# Revit family: Hager-GOLF-Flush_mounted-IP40-With_Cover-With_DIN-NoHosted-DE-de
name_source: partatom
category: Electrical Equipment
units: mm (PartAtom-declared; Revit-internal decimal feet)

## family parameters
Always vertical = Yes
Cut with Voids When Loaded = No
Maintain Annotation Orientation = No
Panel Configuration = Two Columns, Circuits Across
Part Type = Panelboard
Room Calculation Point = No
Round Connector Dimension = Use Diameter
Shared = No
Work Plane-Based = Yes

## types (69) — shared parameters
Code hager = ADD-EC000214_EU
Default Elevation = 1200 mm
EF000003 - Montageart = Unterputz
EF000007 - Farbe = weiß
EF000024 - UV-beständig = No
EF000049 - Tiefe = 97 mm  [stored 0.318241 ft]
EF000116 - RAL-Nummer = 9010
EF000118 - Mit Montageplatte = No
EF000218 - Einbautiefe = 72 mm  [stored 0.23622 ft]
EF001062 - EMV-Ausführung = No
EF001088 - Anbaumöglichkeit = Yes
EF001134 - DIN-Schiene = Yes
EF004462 - Art der Schließung = sonstige
EF005474 - Schutzart (IP) = IP40
EF006306 - Mit Schloss = No
EF009212 - Ausführung Deckel = geschlossen
EF015941 - Signaldurchlassende Tür = Yes
ETIM class code = EC000214
ETIM class name = Small distribution board
HG000001-Anzahl der Spalten = 1
HG000002-Mit tür = Yes
HG000003-Bereich = GOLF
HG000005-Dicke = 2 mm  [stored 0.00656168 ft]
HG000006-Flush mounted = Yes
HG000009-Doppelflügeligen Tür = No
HG000010-Asymmetrische Türen = No
HG000011-Leere Reihen von unten = No
HG000012-Türschwenkwinkel = 90.00°
HG000013-Tür links = No
HG000014-Tür rechts = Yes
HG000015-Sichtbarkeit der Türöffnung = Yes
HG000016-3D-Türsichtbarkeit = Yes
HG000017-Distanz zwischen den Polen = 18 mm  [stored 0.0590551 ft]
HG000060-RAL-number = 9010
HG000099-Onfly Template ID-de-DE = 507532
Manufacturer = Hager
Name BIM&CO = Electricity
Name hager = ADD_Enclosures_EC000214
Reference = Template-Enclosure_EU-EC000214
Uniformat = Low Tension Service & Dist.
Uniformat code = D501001
zero-valued in all types: EF001131 - Innentiefe, HG000007-Anzahl der leeren Spalten, HG000008-Anzahl der leeren Reihen

## per-type parameters (varying)
| type | BC_METADATA | EF000008 - Breite | EF000040 - Höhe | EF000266 - Anzahl der Reihen | EF000332 - Einbauhöhe | EF000846 - Einbaubreite | EF002950 - Breite in Teilungseinheiten | EF006244 - Transparenter Deckel/Tür | EF015776 - Erdungsklemmenblock | EF015777 - Neutralleiterklemmenblock | HG000004-Herstellerreferenz | HGEF000266-Anzahl der Reihen | HGEF0002950-Breite in Teilungseinheiten |
| GOLF-Flush_mounted_W204_H225_D97_4_Modular_Spacing-VF104PD | {"ObjectGuid":"2e7d348a-37d7-415c-a700-8c675d7a2511","ModelGuid":"d92884ee-31d5-45f1-a563-37bca790122f","VariantGuid":"b31a2e9c-c330-4702-bbce-c17fa995467c","Revision":"#5","VariantName":"GOLF-Flush_mounted_W204_H225_D97_4_Modular_Spacing-VF104PD"} | 204 mm | 225 mm  [stored 0.738189 ft] | 1 | 189 mm  [stored 0.620079 ft] | 170 mm  [stored 0.557743 ft] | 4 | No | Yes | Yes | VF104PD | 1 | 4 |
| GOLF-Flush_mounted_W204_H225_D97_4_Modular_Spacing-VF104PS | {"ObjectGuid":"2e7d348a-37d7-415c-a700-8c675d7a2511","ModelGuid":"d92884ee-31d5-45f1-a563-37bca790122f","VariantGuid":"cf317ba9-bf0b-43f1-8adb-6811de942370","Revision":"#5","VariantName":"GOLF-Flush_mounted_W204_H225_D97_4_Modular_Spacing-VF104PS"} | 204 mm | 225 mm  [stored 0.738189 ft] | 1 | 189 mm  [stored 0.620079 ft] | 170 mm  [stored 0.557743 ft] | 4 | No | No | No | VF104PS | 1 | 4 |
| GOLF-Flush_mounted_W204_H225_D97_4_Modular_Spacing-VF104TD | {"ObjectGuid":"2e7d348a-37d7-415c-a700-8c675d7a2511","ModelGuid":"d92884ee-31d5-45f1-a563-37bca790122f","VariantGuid":"4740b172-a5a6-4442-adbc-1241339a5770","Revision":"#5","VariantName":"GOLF-Flush_mounted_W204_H225_D97_4_Modular_Spacing-VF104TD"} | 204 mm | 225 mm  [stored 0.738189 ft] | 1 | 189 mm  [stored 0.620079 ft] | 170 mm  [stored 0.557743 ft] | 4 | Yes | Yes | Yes | VF104TD | 1 | 4 |
| GOLF-Flush_mounted_W204_H225_D97_4_Modular_Spacing-VF104TS | {"ObjectGuid":"2e7d348a-37d7-415c-a700-8c675d7a2511","ModelGuid":"d92884ee-31d5-45f1-a563-37bca790122f","VariantGuid":"b190a470-c8c2-49e1-a780-9f87e2cea34b","Revision":"#5","VariantName":"GOLF-Flush_mounted_W204_H225_D97_4_Modular_Spacing-VF104TS"} | 204 mm | 225 mm  [stored 0.738189 ft] | 1 | 189 mm  [stored 0.620079 ft] | 170 mm  [stored 0.557743 ft] | 4 | Yes | No | No | VF104TS | 1 | 4 |
| GOLF-Flush_mounted_W275_H225_D97_8_Modular_Spacing-VF108PA | {"ObjectGuid":"2e7d348a-37d7-415c-a700-8c675d7a2511","ModelGuid":"d92884ee-31d5-45f1-a563-37bca790122f","VariantGuid":"5aee5411-9867-4517-88c6-ba6237cbbf09","Revision":"#5","VariantName":"GOLF-Flush_mounted_W275_H225_D97_8_Modular_Spacing-VF108PA"} | 275 mm | 225 mm  [stored 0.738189 ft] | 1 | 189 mm  [stored 0.620079 ft] | 242 mm  [stored 0.793963 ft] | 8 | No | Yes | Yes | VF108PA | 1 | 8 |
| GOLF-Flush_mounted_W275_H225_D97_8_Modular_Spacing-VF108PD | {"ObjectGuid":"2e7d348a-37d7-415c-a700-8c675d7a2511","ModelGuid":"d92884ee-31d5-45f1-a563-37bca790122f","VariantGuid":"886cf811-8d76-449f-90a1-8f1109ad9289","Revision":"#5","VariantName":"GOLF-Flush_mounted_W275_H225_D97_8_Modular_Spacing-VF108PD"} | 275 mm | 225 mm  [stored 0.738189 ft] | 1 | 189 mm  [stored 0.620079 ft] | 242 mm  [stored 0.793963 ft] | 8 | No | Yes | Yes | VF108PD | 1 | 8 |
| GOLF-Flush_mounted_W275_H225_D97_8_Modular_Spacing-VF108PS | {"ObjectGuid":"2e7d348a-37d7-415c-a700-8c675d7a2511","ModelGuid":"d92884ee-31d5-45f1-a563-37bca790122f","VariantGuid":"b0350e41-627a-4a22-b8d4-8089ab5dced8","Revision":"#5","VariantName":"GOLF-Flush_mounted_W275_H225_D97_8_Modular_Spacing-VF108PS"} | 275 mm | 225 mm  [stored 0.738189 ft] | 1 | 189 mm  [stored 0.620079 ft] | 242 mm  [stored 0.793963 ft] | 8 | No | No | No | VF108PS | 1 | 8 |
| GOLF-Flush_mounted_W275_H225_D97_8_Modular_Spacing-VF108TA | {"ObjectGuid":"2e7d348a-37d7-415c-a700-8c675d7a2511","ModelGuid":"d92884ee-31d5-45f1-a563-37bca790122f","VariantGuid":"434fecd7-12d2-4bc4-95db-9da8fda5b05a","Revision":"#5","VariantName":"GOLF-Flush_mounted_W275_H225_D97_8_Modular_Spacing-VF108TA"} | 275 mm | 225 mm  [stored 0.738189 ft] | 1 | 189 mm  [stored 0.620079 ft] | 242 mm  [stored 0.793963 ft] | 8 | Yes | Yes | Yes | VF108TA | 1 | 8 |
| GOLF-Flush_mounted_W275_H225_D97_8_Modular_Spacing-VF108TD | {"ObjectGuid":"2e7d348a-37d7-415c-a700-8c675d7a2511","ModelGuid":"d92884ee-31d5-45f1-a563-37bca790122f","VariantGuid":"33042274-c18e-4c81-9396-54769ed373ac","Revision":"#5","VariantName":"GOLF-Flush_mounted_W275_H225_D97_8_Modular_Spacing-VF108TD"} | 275 mm | 225 mm  [stored 0.738189 ft] | 1 | 189 mm  [stored 0.620079 ft] | 242 mm  [stored 0.793963 ft] | 8 | Yes | Yes | Yes | VF108TD | 1 | 8 |
| GOLF-Flush_mounted_W275_H225_D97_8_Modular_Spacing-VF108TJ | {"ObjectGuid":"2e7d348a-37d7-415c-a700-8c675d7a2511","ModelGuid":"d92884ee-31d5-45f1-a563-37bca790122f","VariantGuid":"0d447c01-cd4f-45ee-b8f3-b86ee1e16cdc","Revision":"#5","VariantName":"GOLF-Flush_mounted_W275_H225_D97_8_Modular_Spacing-VF108TJ"} | 275 mm | 225 mm  [stored 0.738189 ft] | 1 | 189 mm  [stored 0.620079 ft] | 242 mm  [stored 0.793963 ft] | 8 | Yes | Yes | Yes | VF108TJ | 1 | 8 |
| GOLF-Flush_mounted_W275_H225_D97_8_Modular_Spacing-VF108TS | {"ObjectGuid":"2e7d348a-37d7-415c-a700-8c675d7a2511","ModelGuid":"d92884ee-31d5-45f1-a563-37bca790122f","VariantGuid":"a07ff41f-50ed-4bbd-adef-f6161eaefa04","Revision":"#5","VariantName":"GOLF-Flush_mounted_W275_H225_D97_8_Modular_Spacing-VF108TS"} | 275 mm | 225 mm  [stored 0.738189 ft] | 1 | 189 mm  [stored 0.620079 ft] | 242 mm  [stored 0.793963 ft] | 8 | Yes | No | No | VF108TS | 1 | 8 |
| GOLF-Flush_mounted_W352_H293_D97_12_Modular_Spacing-VF112PD | {"ObjectGuid":"2e7d348a-37d7-415c-a700-8c675d7a2511","ModelGuid":"d92884ee-31d5-45f1-a563-37bca790122f","VariantGuid":"0fa4f423-8072-41b0-9108-ada0960ab0c6","Revision":"#5","VariantName":"GOLF-Flush_mounted_W352_H293_D97_12_Modular_Spacing-VF112PD"} | 352 mm  [stored 1.15486 ft] | 293 mm | 1 | 257 mm  [stored 0.843176 ft] | 318 mm  [stored 1.04331 ft] | 12 | No | Yes | Yes | VF112PD | 1 | 12 |
| GOLF-Flush_mounted_W352_H293_D97_12_Modular_Spacing-VF112PF | {"ObjectGuid":"2e7d348a-37d7-415c-a700-8c675d7a2511","ModelGuid":"d92884ee-31d5-45f1-a563-37bca790122f","VariantGuid":"cda2493f-6014-4af5-b370-7196b7a504cb","Revision":"#5","VariantName":"GOLF-Flush_mounted_W352_H293_D97_12_Modular_Spacing-VF112PF"} | 352 mm  [stored 1.15486 ft] | 293 mm | 1 | 257 mm  [stored 0.843176 ft] | 318 mm  [stored 1.04331 ft] | 12 | No | Yes | No | VF112PF | 1 | 12 |
| GOLF-Flush_mounted_W352_H293_D97_12_Modular_Spacing-VF112PJ | {"ObjectGuid":"2e7d348a-37d7-415c-a700-8c675d7a2511","ModelGuid":"d92884ee-31d5-45f1-a563-37bca790122f","VariantGuid":"3e67deef-0626-41d4-b3ad-e567f991c98e","Revision":"#5","VariantName":"GOLF-Flush_mounted_W352_H293_D97_12_Modular_Spacing-VF112PJ"} | 352 mm  [stored 1.15486 ft] | 293 mm | 1 | 257 mm  [stored 0.843176 ft] | 318 mm  [stored 1.04331 ft] | 12 | No | Yes | Yes | VF112PJ | 1 | 12 |
| GOLF-Flush_mounted_W352_H293_D97_12_Modular_Spacing-VF112PS | {"ObjectGuid":"2e7d348a-37d7-415c-a700-8c675d7a2511","ModelGuid":"d92884ee-31d5-45f1-a563-37bca790122f","VariantGuid":"aa0eb0c4-cc24-4b40-a068-d6b0dbcf8f14","Revision":"#5","VariantName":"GOLF-Flush_mounted_W352_H293_D97_12_Modular_Spacing-VF112PS"} | 352 mm  [stored 1.15486 ft] | 293 mm | 1 | 257 mm  [stored 0.843176 ft] | 318 mm  [stored 1.04331 ft] | 12 | No | Yes | Yes | VF112PS | 1 | 12 |
| GOLF-Flush_mounted_W352_H293_D97_12_Modular_Spacing-VF112TD | {"ObjectGuid":"2e7d348a-37d7-415c-a700-8c675d7a2511","ModelGuid":"d92884ee-31d5-45f1-a563-37bca790122f","VariantGuid":"c066e9c2-883b-4a27-bd66-81f75bf34be1","Revision":"#5","VariantName":"GOLF-Flush_mounted_W352_H293_D97_12_Modular_Spacing-VF112TD"} | 352 mm  [stored 1.15486 ft] | 293 mm | 1 | 257 mm  [stored 0.843176 ft] | 318 mm  [stored 1.04331 ft] | 12 | Yes | Yes | Yes | VF112TD | 1 | 12 |
| GOLF-Flush_mounted_W352_H293_D97_12_Modular_Spacing-VF112TJ | {"ObjectGuid":"2e7d348a-37d7-415c-a700-8c675d7a2511","ModelGuid":"d92884ee-31d5-45f1-a563-37bca790122f","VariantGuid":"6bc9c1f8-911c-4ce2-a106-367671bf1206","Revision":"#5","VariantName":"GOLF-Flush_mounted_W352_H293_D97_12_Modular_Spacing-VF112TJ"} | 352 mm  [stored 1.15486 ft] | 293 mm | 1 | 257 mm  [stored 0.843176 ft] | 318 mm  [stored 1.04331 ft] | 12 | Yes | Yes | Yes | VF112TJ | 1 | 12 |
| GOLF-Flush_mounted_W352_H293_D97_12_Modular_Spacing-VF112TS | {"ObjectGuid":"2e7d348a-37d7-415c-a700-8c675d7a2511","ModelGuid":"d92884ee-31d5-45f1-a563-37bca790122f","VariantGuid":"ad58a622-cc60-446c-a541-a335049a2472","Revision":"#5","VariantName":"GOLF-Flush_mounted_W352_H293_D97_12_Modular_Spacing-VF112TS"} | 352 mm  [stored 1.15486 ft] | 293 mm | 1 | 257 mm  [stored 0.843176 ft] | 318 mm  [stored 1.04331 ft] | 12 | Yes | Yes | Yes | VF112TS | 1 | 12 |
| GOLF-Flush_mounted_W460_H293_D97_18_Modular_Spacing-VF118PD | {"ObjectGuid":"2e7d348a-37d7-415c-a700-8c675d7a2511","ModelGuid":"d92884ee-31d5-45f1-a563-37bca790122f","VariantGuid":"105932b2-cbf7-41df-8ac9-181a1f292d99","Revision":"#5","VariantName":"GOLF-Flush_mounted_W460_H293_D97_18_Modular_Spacing-VF118PD"} | 460 mm  [stored 1.50919 ft] | 293 mm | 1 | 257 mm  [stored 0.843176 ft] | 426 mm  [stored 1.39764 ft] | 18 | No | Yes | Yes | VF118PD | 1 | 18 |
| GOLF-Flush_mounted_W460_H293_D97_18_Modular_Spacing-VF118PJ | {"ObjectGuid":"2e7d348a-37d7-415c-a700-8c675d7a2511","ModelGuid":"d92884ee-31d5-45f1-a563-37bca790122f","VariantGuid":"70001ed9-ceb5-4983-a4dc-93935931aaab","Revision":"#5","VariantName":"GOLF-Flush_mounted_W460_H293_D97_18_Modular_Spacing-VF118PJ"} | 460 mm  [stored 1.50919 ft] | 293 mm | 1 | 257 mm  [stored 0.843176 ft] | 426 mm  [stored 1.39764 ft] | 18 | No | Yes | Yes | VF118PJ | 1 | 18 |
| GOLF-Flush_mounted_W460_H293_D97_18_Modular_Spacing-VF118PS | {"ObjectGuid":"2e7d348a-37d7-415c-a700-8c675d7a2511","ModelGuid":"d92884ee-31d5-45f1-a563-37bca790122f","VariantGuid":"d0a27ae8-1dc5-4747-8d64-8ad361803e2f","Revision":"#5","VariantName":"GOLF-Flush_mounted_W460_H293_D97_18_Modular_Spacing-VF118PS"} | 460 mm  [stored 1.50919 ft] | 293 mm | 1 | 257 mm  [stored 0.843176 ft] | 426 mm  [stored 1.39764 ft] | 18 | No | Yes | Yes | VF118PS | 1 | 18 |
| GOLF-Flush_mounted_W460_H293_D97_18_Modular_Spacing-VF118TD | {"ObjectGuid":"2e7d348a-37d7-415c-a700-8c675d7a2511","ModelGuid":"d92884ee-31d5-45f1-a563-37bca790122f","VariantGuid":"fbfa0a9f-1e1a-4261-a0f8-0ef638ea11ae","Revision":"#5","VariantName":"GOLF-Flush_mounted_W460_H293_D97_18_Modular_Spacing-VF118TD"} | 460 mm  [stored 1.50919 ft] | 293 mm | 1 | 257 mm  [stored 0.843176 ft] | 426 mm  [stored 1.39764 ft] | 18 | Yes | Yes | Yes | VF118TD | 1 | 18 |
| GOLF-Flush_mounted_W460_H293_D97_18_Modular_Spacing-VF118TJ | {"ObjectGuid":"2e7d348a-37d7-415c-a700-8c675d7a2511","ModelGuid":"d92884ee-31d5-45f1-a563-37bca790122f","VariantGuid":"94245f96-ff7b-4568-9343-245a51ee46bc","Revision":"#5","VariantName":"GOLF-Flush_mounted_W460_H293_D97_18_Modular_Spacing-VF118TJ"} | 460 mm  [stored 1.50919 ft] | 293 mm | 1 | 257 mm  [stored 0.843176 ft] | 426 mm  [stored 1.39764 ft] | 18 | Yes | Yes | Yes | VF118TJ | 1 | 18 |
| GOLF-Flush_mounted_W460_H293_D97_18_Modular_Spacing-VF118TS | {"ObjectGuid":"2e7d348a-37d7-415c-a700-8c675d7a2511","ModelGuid":"d92884ee-31d5-45f1-a563-37bca790122f","VariantGuid":"0d8941fe-6963-4aca-883e-c03dfea5f93c","Revision":"#5","VariantName":"GOLF-Flush_mounted_W460_H293_D97_18_Modular_Spacing-VF118TS"} | 460 mm  [stored 1.50919 ft] | 293 mm | 1 | 257 mm  [stored 0.843176 ft] | 426 mm  [stored 1.39764 ft] | 18 | Yes | Yes | Yes | VF118TS | 1 | 18 |
| GOLF-Flush_mounted_W532_H293_D97_22_Modular_Spacing-VF122PD | {"ObjectGuid":"2e7d348a-37d7-415c-a700-8c675d7a2511","ModelGuid":"d92884ee-31d5-45f1-a563-37bca790122f","VariantGuid":"ca360b59-2ed4-4731-9d1a-494a27b09c55","Revision":"#5","VariantName":"GOLF-Flush_mounted_W532_H293_D97_22_Modular_Spacing-VF122PD"} | 532 mm  [stored 1.74541 ft] | 293 mm | 1 | 257 mm  [stored 0.843176 ft] | 498 mm  [stored 1.63386 ft] | 22 | No | Yes | Yes | VF122PD | 1 | 22 |
| GOLF-Flush_mounted_W532_H293_D97_22_Modular_Spacing-VF122PJ | {"ObjectGuid":"2e7d348a-37d7-415c-a700-8c675d7a2511","ModelGuid":"d92884ee-31d5-45f1-a563-37bca790122f","VariantGuid":"9e92291c-d38c-4a34-8822-f9d752054a3e","Revision":"#5","VariantName":"GOLF-Flush_mounted_W532_H293_D97_22_Modular_Spacing-VF122PJ"} | 532 mm  [stored 1.74541 ft] | 293 mm | 1 | 257 mm  [stored 0.843176 ft] | 498 mm  [stored 1.63386 ft] | 22 | No | Yes | Yes | VF122PJ | 1 | 22 |
| GOLF-Flush_mounted_W532_H293_D97_22_Modular_Spacing-VF122PS | {"ObjectGuid":"2e7d348a-37d7-415c-a700-8c675d7a2511","ModelGuid":"d92884ee-31d5-45f1-a563-37bca790122f","VariantGuid":"727b1c2d-92bc-408c-a085-bd908a56903f","Revision":"#5","VariantName":"GOLF-Flush_mounted_W532_H293_D97_22_Modular_Spacing-VF122PS"} | 532 mm  [stored 1.74541 ft] | 293 mm | 1 | 257 mm  [stored 0.843176 ft] | 498 mm  [stored 1.63386 ft] | 22 | No | Yes | Yes | VF122PS | 1 | 22 |
| GOLF-Flush_mounted_W532_H293_D97_22_Modular_Spacing-VF122TD | {"ObjectGuid":"2e7d348a-37d7-415c-a700-8c675d7a2511","ModelGuid":"d92884ee-31d5-45f1-a563-37bca790122f","VariantGuid":"9d93141a-b6ba-4929-b79b-eee7cde6022e","Revision":"#5","VariantName":"GOLF-Flush_mounted_W532_H293_D97_22_Modular_Spacing-VF122TD"} | 532 mm  [stored 1.74541 ft] | 293 mm | 1 | 257 mm  [stored 0.843176 ft] | 498 mm  [stored 1.63386 ft] | 22 | Yes | Yes | Yes | VF122TD | 1 | 22 |
| GOLF-Flush_mounted_W532_H293_D97_22_Modular_Spacing-VF122TJ | {"ObjectGuid":"2e7d348a-37d7-415c-a700-8c675d7a2511","ModelGuid":"d92884ee-31d5-45f1-a563-37bca790122f","VariantGuid":"dadf0be1-38d8-4523-8671-6e9106750640","Revision":"#5","VariantName":"GOLF-Flush_mounted_W532_H293_D97_22_Modular_Spacing-VF122TJ"} | 532 mm  [stored 1.74541 ft] | 293 mm | 1 | 257 mm  [stored 0.843176 ft] | 498 mm  [stored 1.63386 ft] | 22 | Yes | Yes | Yes | VF122TJ | 1 | 22 |
| GOLF-Flush_mounted_W532_H293_D97_22_Modular_Spacing-VF122TS | {"ObjectGuid":"2e7d348a-37d7-415c-a700-8c675d7a2511","ModelGuid":"d92884ee-31d5-45f1-a563-37bca790122f","VariantGuid":"bc3eb722-4a62-46bc-8f7d-958ac2879342","Revision":"#5","VariantName":"GOLF-Flush_mounted_W532_H293_D97_22_Modular_Spacing-VF122TS"} | 532 mm  [stored 1.74541 ft] | 293 mm | 1 | 257 mm  [stored 0.843176 ft] | 498 mm  [stored 1.63386 ft] | 22 | Yes | Yes | Yes | VF122TS | 1 | 22 |
| GOLF-Flush_mounted_W382_H418_D97_12_Modular_Spacing-VF212PD | {"ObjectGuid":"2e7d348a-37d7-415c-a700-8c675d7a2511","ModelGuid":"d92884ee-31d5-45f1-a563-37bca790122f","VariantGuid":"98662327-9122-4b4b-b095-2d9bc4e226c7","Revision":"#5","VariantName":"GOLF-Flush_mounted_W382_H418_D97_12_Modular_Spacing-VF212PD"} | 382 mm  [stored 1.25328 ft] | 418 mm  [stored 1.37139 ft] | 2 | 382 mm  [stored 1.25328 ft] | 318 mm  [stored 1.04331 ft] | 12 | No | Yes | Yes | VF212PD | 2 | 12 |
| GOLF-Flush_mounted_W382_H418_D97_12_Modular_Spacing-VF212PF | {"ObjectGuid":"2e7d348a-37d7-415c-a700-8c675d7a2511","ModelGuid":"d92884ee-31d5-45f1-a563-37bca790122f","VariantGuid":"4c255126-cffe-43da-86a0-3f511cb3c73b","Revision":"#5","VariantName":"GOLF-Flush_mounted_W382_H418_D97_12_Modular_Spacing-VF212PF"} | 382 mm  [stored 1.25328 ft] | 418 mm  [stored 1.37139 ft] | 2 | 382 mm  [stored 1.25328 ft] | 318 mm  [stored 1.04331 ft] | 12 | No | Yes | No | VF212PF | 2 | 12 |
| GOLF-Flush_mounted_W382_H418_D97_12_Modular_Spacing-VF212PJ | {"ObjectGuid":"2e7d348a-37d7-415c-a700-8c675d7a2511","ModelGuid":"d92884ee-31d5-45f1-a563-37bca790122f","VariantGuid":"0282bb31-53a3-40e4-a5f7-7024e7f81640","Revision":"#5","VariantName":"GOLF-Flush_mounted_W382_H418_D97_12_Modular_Spacing-VF212PJ"} | 382 mm  [stored 1.25328 ft] | 418 mm  [stored 1.37139 ft] | 2 | 382 mm  [stored 1.25328 ft] | 318 mm  [stored 1.04331 ft] | 12 | No | Yes | Yes | VF212PJ | 2 | 12 |
| GOLF-Flush_mounted_W382_H418_D97_12_Modular_Spacing-VF212PS | {"ObjectGuid":"2e7d348a-37d7-415c-a700-8c675d7a2511","ModelGuid":"d92884ee-31d5-45f1-a563-37bca790122f","VariantGuid":"ee81c795-a8c6-4e0b-ac30-7d2952e06c4c","Revision":"#5","VariantName":"GOLF-Flush_mounted_W382_H418_D97_12_Modular_Spacing-VF212PS"} | 382 mm  [stored 1.25328 ft] | 418 mm  [stored 1.37139 ft] | 2 | 382 mm  [stored 1.25328 ft] | 318 mm  [stored 1.04331 ft] | 12 | No | Yes | Yes | VF212PS | 2 | 12 |
| GOLF-Flush_mounted_W382_H418_D97_12_Modular_Spacing-VF212TA | {"ObjectGuid":"2e7d348a-37d7-415c-a700-8c675d7a2511","ModelGuid":"d92884ee-31d5-45f1-a563-37bca790122f","VariantGuid":"6bae1c2d-9032-4d60-8b30-56f41d07c7fb","Revision":"#5","VariantName":"GOLF-Flush_mounted_W382_H418_D97_12_Modular_Spacing-VF212TA"} | 382 mm  [stored 1.25328 ft] | 418 mm  [stored 1.37139 ft] | 2 | 382 mm  [stored 1.25328 ft] | 318 mm  [stored 1.04331 ft] | 12 | Yes | Yes | Yes | VF212TA | 2 | 12 |
| GOLF-Flush_mounted_W382_H418_D97_12_Modular_Spacing-VF212TD | {"ObjectGuid":"2e7d348a-37d7-415c-a700-8c675d7a2511","ModelGuid":"d92884ee-31d5-45f1-a563-37bca790122f","VariantGuid":"fe428a60-72be-47c5-b277-cfdae7ead9f2","Revision":"#5","VariantName":"GOLF-Flush_mounted_W382_H418_D97_12_Modular_Spacing-VF212TD"} | 382 mm  [stored 1.25328 ft] | 418 mm  [stored 1.37139 ft] | 2 | 382 mm  [stored 1.25328 ft] | 318 mm  [stored 1.04331 ft] | 12 | Yes | Yes | Yes | VF212TD | 2 | 12 |
| GOLF-Flush_mounted_W382_H418_D97_12_Modular_Spacing-VF212TJ | {"ObjectGuid":"2e7d348a-37d7-415c-a700-8c675d7a2511","ModelGuid":"d92884ee-31d5-45f1-a563-37bca790122f","VariantGuid":"4d1ea7fb-c5ff-44ed-a8ff-c7a03550a839","Revision":"#5","VariantName":"GOLF-Flush_mounted_W382_H418_D97_12_Modular_Spacing-VF212TJ"} | 382 mm  [stored 1.25328 ft] | 418 mm  [stored 1.37139 ft] | 2 | 382 mm  [stored 1.25328 ft] | 318 mm  [stored 1.04331 ft] | 12 | Yes | Yes | Yes | VF212TJ | 2 | 12 |
| GOLF-Flush_mounted_W382_H418_D97_12_Modular_Spacing-VF212TS | {"ObjectGuid":"2e7d348a-37d7-415c-a700-8c675d7a2511","ModelGuid":"d92884ee-31d5-45f1-a563-37bca790122f","VariantGuid":"0f97c2f5-fb0b-4114-b1b1-1e9c94daf7b6","Revision":"#5","VariantName":"GOLF-Flush_mounted_W382_H418_D97_12_Modular_Spacing-VF212TS"} | 382 mm  [stored 1.25328 ft] | 418 mm  [stored 1.37139 ft] | 2 | 382 mm  [stored 1.25328 ft] | 318 mm  [stored 1.04331 ft] | 12 | Yes | Yes | Yes | VF212TS | 2 | 12 |
| GOLF-Flush_mounted_W460_H418_D97_18_Modular_Spacing-VF218PD | {"ObjectGuid":"2e7d348a-37d7-415c-a700-8c675d7a2511","ModelGuid":"d92884ee-31d5-45f1-a563-37bca790122f","VariantGuid":"99250fe5-2cb4-4589-b5fd-ac7613f56618","Revision":"#5","VariantName":"GOLF-Flush_mounted_W460_H418_D97_18_Modular_Spacing-VF218PD"} | 460 mm  [stored 1.50919 ft] | 418 mm  [stored 1.37139 ft] | 2 | 382 mm  [stored 1.25328 ft] | 426 mm  [stored 1.39764 ft] | 18 | No | Yes | Yes | VF218PD | 2 | 18 |
| GOLF-Flush_mounted_W460_H418_D97_18_Modular_Spacing-VF218PJ | {"ObjectGuid":"2e7d348a-37d7-415c-a700-8c675d7a2511","ModelGuid":"d92884ee-31d5-45f1-a563-37bca790122f","VariantGuid":"c85930e7-9cfc-47db-97e7-0fb22923e959","Revision":"#5","VariantName":"GOLF-Flush_mounted_W460_H418_D97_18_Modular_Spacing-VF218PJ"} | 460 mm  [stored 1.50919 ft] | 418 mm  [stored 1.37139 ft] | 2 | 382 mm  [stored 1.25328 ft] | 426 mm  [stored 1.39764 ft] | 18 | No | Yes | Yes | VF218PJ | 2 | 18 |
| GOLF-Flush_mounted_W460_H418_D97_18_Modular_Spacing-VF218PS | {"ObjectGuid":"2e7d348a-37d7-415c-a700-8c675d7a2511","ModelGuid":"d92884ee-31d5-45f1-a563-37bca790122f","VariantGuid":"cbc02418-1134-4bb1-abc3-8cda3f068379","Revision":"#5","VariantName":"GOLF-Flush_mounted_W460_H418_D97_18_Modular_Spacing-VF218PS"} | 460 mm  [stored 1.50919 ft] | 418 mm  [stored 1.37139 ft] | 2 | 382 mm  [stored 1.25328 ft] | 426 mm  [stored 1.39764 ft] | 18 | No | Yes | Yes | VF218PS | 2 | 18 |
| GOLF-Flush_mounted_W460_H418_D97_18_Modular_Spacing-VF218TD | {"ObjectGuid":"2e7d348a-37d7-415c-a700-8c675d7a2511","ModelGuid":"d92884ee-31d5-45f1-a563-37bca790122f","VariantGuid":"913d6e5d-7559-403e-89d5-0aa80b5e0efb","Revision":"#5","VariantName":"GOLF-Flush_mounted_W460_H418_D97_18_Modular_Spacing-VF218TD"} | 460 mm  [stored 1.50919 ft] | 418 mm  [stored 1.37139 ft] | 2 | 382 mm  [stored 1.25328 ft] | 426 mm  [stored 1.39764 ft] | 18 | Yes | Yes | Yes | VF218TD | 2 | 18 |
| GOLF-Flush_mounted_W460_H418_D97_18_Modular_Spacing-VF218TJ | {"ObjectGuid":"2e7d348a-37d7-415c-a700-8c675d7a2511","ModelGuid":"d92884ee-31d5-45f1-a563-37bca790122f","VariantGuid":"6aa5c099-a717-4ea1-8fc0-bc053faefae9","Revision":"#5","VariantName":"GOLF-Flush_mounted_W460_H418_D97_18_Modular_Spacing-VF218TJ"} | 460 mm  [stored 1.50919 ft] | 418 mm  [stored 1.37139 ft] | 2 | 382 mm  [stored 1.25328 ft] | 426 mm  [stored 1.39764 ft] | 18 | Yes | Yes | Yes | VF218TJ | 2 | 18 |
| GOLF-Flush_mounted_W460_H418_D97_18_Modular_Spacing-VF218TS | {"ObjectGuid":"2e7d348a-37d7-415c-a700-8c675d7a2511","ModelGuid":"d92884ee-31d5-45f1-a563-37bca790122f","VariantGuid":"8aefd23b-b0b6-4d46-847b-f36bf3c04371","Revision":"#5","VariantName":"GOLF-Flush_mounted_W460_H418_D97_18_Modular_Spacing-VF218TS"} | 460 mm  [stored 1.50919 ft] | 418 mm  [stored 1.37139 ft] | 2 | 382 mm  [stored 1.25328 ft] | 426 mm  [stored 1.39764 ft] | 18 | Yes | Yes | Yes | VF218TS | 2 | 18 |
| GOLF-Flush_mounted_W352_H543_D97_12_Modular_Spacing-VF312PD | {"ObjectGuid":"2e7d348a-37d7-415c-a700-8c675d7a2511","ModelGuid":"d92884ee-31d5-45f1-a563-37bca790122f","VariantGuid":"928b9372-45b5-4d68-aaf5-065da6247f86","Revision":"#5","VariantName":"GOLF-Flush_mounted_W352_H543_D97_12_Modular_Spacing-VF312PD"} | 352 mm  [stored 1.15486 ft] | 543 mm  [stored 1.7815 ft] | 3 | 507 mm  [stored 1.66339 ft] | 318 mm  [stored 1.04331 ft] | 12 | No | Yes | Yes | VF312PD | 3 | 12 |
| GOLF-Flush_mounted_W352_H543_D97_12_Modular_Spacing-VF312PF | {"ObjectGuid":"2e7d348a-37d7-415c-a700-8c675d7a2511","ModelGuid":"d92884ee-31d5-45f1-a563-37bca790122f","VariantGuid":"b4990f75-6e65-45c0-bd5a-b16e10202182","Revision":"#5","VariantName":"GOLF-Flush_mounted_W352_H543_D97_12_Modular_Spacing-VF312PF"} | 352 mm  [stored 1.15486 ft] | 543 mm  [stored 1.7815 ft] | 3 | 507 mm  [stored 1.66339 ft] | 318 mm  [stored 1.04331 ft] | 12 | No | Yes | No | VF312PF | 3 | 12 |
| GOLF-Flush_mounted_W352_H543_D97_12_Modular_Spacing-VF312PJ | {"ObjectGuid":"2e7d348a-37d7-415c-a700-8c675d7a2511","ModelGuid":"d92884ee-31d5-45f1-a563-37bca790122f","VariantGuid":"a1a3ce38-9ed2-44bf-af35-44c8f29b8579","Revision":"#5","VariantName":"GOLF-Flush_mounted_W352_H543_D97_12_Modular_Spacing-VF312PJ"} | 352 mm  [stored 1.15486 ft] | 543 mm  [stored 1.7815 ft] | 3 | 507 mm  [stored 1.66339 ft] | 318 mm  [stored 1.04331 ft] | 12 | No | Yes | Yes | VF312PJ | 3 | 12 |
| GOLF-Flush_mounted_W352_H543_D97_12_Modular_Spacing-VF312PS | {"ObjectGuid":"2e7d348a-37d7-415c-a700-8c675d7a2511","ModelGuid":"d92884ee-31d5-45f1-a563-37bca790122f","VariantGuid":"8e26eca7-dae5-4654-a159-605baed50f82","Revision":"#5","VariantName":"GOLF-Flush_mounted_W352_H543_D97_12_Modular_Spacing-VF312PS"} | 352 mm  [stored 1.15486 ft] | 543 mm  [stored 1.7815 ft] | 3 | 507 mm  [stored 1.66339 ft] | 318 mm  [stored 1.04331 ft] | 12 | No | Yes | Yes | VF312PS | 3 | 12 |
| GOLF-Flush_mounted_W352_H543_D97_12_Modular_Spacing-VF312TD | {"ObjectGuid":"2e7d348a-37d7-415c-a700-8c675d7a2511","ModelGuid":"d92884ee-31d5-45f1-a563-37bca790122f","VariantGuid":"48a651ff-040d-4527-aaab-b8df4a12e4b1","Revision":"#5","VariantName":"GOLF-Flush_mounted_W352_H543_D97_12_Modular_Spacing-VF312TD"} | 352 mm  [stored 1.15486 ft] | 543 mm  [stored 1.7815 ft] | 3 | 507 mm  [stored 1.66339 ft] | 318 mm  [stored 1.04331 ft] | 12 | Yes | Yes | Yes | VF312TD | 3 | 12 |
| GOLF-Flush_mounted_W352_H543_D97_12_Modular_Spacing-VF312TJ | {"ObjectGuid":"2e7d348a-37d7-415c-a700-8c675d7a2511","ModelGuid":"d92884ee-31d5-45f1-a563-37bca790122f","VariantGuid":"5769b36b-8467-4e38-b90c-6bff2941fc0c","Revision":"#5","VariantName":"GOLF-Flush_mounted_W352_H543_D97_12_Modular_Spacing-VF312TJ"} | 352 mm  [stored 1.15486 ft] | 543 mm  [stored 1.7815 ft] | 3 | 507 mm  [stored 1.66339 ft] | 318 mm  [stored 1.04331 ft] | 12 | Yes | Yes | Yes | VF312TJ | 3 | 12 |
| GOLF-Flush_mounted_W352_H543_D97_12_Modular_Spacing-VF312TS | {"ObjectGuid":"2e7d348a-37d7-415c-a700-8c675d7a2511","ModelGuid":"d92884ee-31d5-45f1-a563-37bca790122f","VariantGuid":"65151222-fdd9-4b8f-85c7-0e54bdfdcd5f","Revision":"#5","VariantName":"GOLF-Flush_mounted_W352_H543_D97_12_Modular_Spacing-VF312TS"} | 352 mm  [stored 1.15486 ft] | 543 mm  [stored 1.7815 ft] | 3 | 507 mm  [stored 1.66339 ft] | 318 mm  [stored 1.04331 ft] | 12 | Yes | Yes | Yes | VF312TS | 3 | 12 |
| GOLF-Flush_mounted_W460_H543_D97_18_Modular_Spacing-VF318PD | {"ObjectGuid":"2e7d348a-37d7-415c-a700-8c675d7a2511","ModelGuid":"d92884ee-31d5-45f1-a563-37bca790122f","VariantGuid":"9ea6dfa0-d29b-4304-aee7-7a29b1dce99d","Revision":"#5","VariantName":"GOLF-Flush_mounted_W460_H543_D97_18_Modular_Spacing-VF318PD"} | 460 mm  [stored 1.50919 ft] | 543 mm  [stored 1.7815 ft] | 3 | 507 mm  [stored 1.66339 ft] | 426 mm  [stored 1.39764 ft] | 18 | No | Yes | Yes | VF318PD | 3 | 18 |
| GOLF-Flush_mounted_W460_H543_D97_18_Modular_Spacing-VF318PJ | {"ObjectGuid":"2e7d348a-37d7-415c-a700-8c675d7a2511","ModelGuid":"d92884ee-31d5-45f1-a563-37bca790122f","VariantGuid":"5d8ebd72-7322-4c37-a4d5-e73088a7ca38","Revision":"#5","VariantName":"GOLF-Flush_mounted_W460_H543_D97_18_Modular_Spacing-VF318PJ"} | 460 mm  [stored 1.50919 ft] | 543 mm  [stored 1.7815 ft] | 3 | 507 mm  [stored 1.66339 ft] | 426 mm  [stored 1.39764 ft] | 18 | No | Yes | Yes | VF318PJ | 3 | 18 |
| GOLF-Flush_mounted_W460_H543_D97_18_Modular_Spacing-VF318PS | {"ObjectGuid":"2e7d348a-37d7-415c-a700-8c675d7a2511","ModelGuid":"d92884ee-31d5-45f1-a563-37bca790122f","VariantGuid":"5c6ad0df-804f-4d99-90e6-483a27ba6c35","Revision":"#5","VariantName":"GOLF-Flush_mounted_W460_H543_D97_18_Modular_Spacing-VF318PS"} | 460 mm  [stored 1.50919 ft] | 543 mm  [stored 1.7815 ft] | 3 | 507 mm  [stored 1.66339 ft] | 426 mm  [stored 1.39764 ft] | 18 | No | Yes | Yes | VF318PS | 3 | 18 |
| GOLF-Flush_mounted_W460_H543_D97_18_Modular_Spacing-VF318TD | {"ObjectGuid":"2e7d348a-37d7-415c-a700-8c675d7a2511","ModelGuid":"d92884ee-31d5-45f1-a563-37bca790122f","VariantGuid":"2c1dced4-bc37-4385-aeb4-8b4dd030778b","Revision":"#5","VariantName":"GOLF-Flush_mounted_W460_H543_D97_18_Modular_Spacing-VF318TD"} | 460 mm  [stored 1.50919 ft] | 543 mm  [stored 1.7815 ft] | 3 | 507 mm  [stored 1.66339 ft] | 426 mm  [stored 1.39764 ft] | 18 | Yes | Yes | Yes | VF318TD | 3 | 18 |
| GOLF-Flush_mounted_W460_H543_D97_18_Modular_Spacing-VF318TJ | {"ObjectGuid":"2e7d348a-37d7-415c-a700-8c675d7a2511","ModelGuid":"d92884ee-31d5-45f1-a563-37bca790122f","VariantGuid":"ca397d7b-ebee-4cf5-97ee-819891202b1a","Revision":"#5","VariantName":"GOLF-Flush_mounted_W460_H543_D97_18_Modular_Spacing-VF318TJ"} | 460 mm  [stored 1.50919 ft] | 543 mm  [stored 1.7815 ft] | 3 | 507 mm  [stored 1.66339 ft] | 426 mm  [stored 1.39764 ft] | 18 | Yes | Yes | Yes | VF318TJ | 3 | 18 |
| GOLF-Flush_mounted_W460_H543_D97_18_Modular_Spacing-VF318TS | {"ObjectGuid":"2e7d348a-37d7-415c-a700-8c675d7a2511","ModelGuid":"d92884ee-31d5-45f1-a563-37bca790122f","VariantGuid":"1c01b16a-0508-4a68-8f02-c14734786524","Revision":"#5","VariantName":"GOLF-Flush_mounted_W460_H543_D97_18_Modular_Spacing-VF318TS"} | 460 mm  [stored 1.50919 ft] | 543 mm  [stored 1.7815 ft] | 3 | 507 mm  [stored 1.66339 ft] | 426 mm  [stored 1.39764 ft] | 18 | Yes | Yes | Yes | VF318TS | 3 | 18 |
| GOLF-Flush_mounted_W352_H688_D97_12_Modular_Spacing-VF412PD | {"ObjectGuid":"2e7d348a-37d7-415c-a700-8c675d7a2511","ModelGuid":"d92884ee-31d5-45f1-a563-37bca790122f","VariantGuid":"49474903-83eb-41eb-8513-ab2748865e8c","Revision":"#5","VariantName":"GOLF-Flush_mounted_W352_H688_D97_12_Modular_Spacing-VF412PD"} | 352 mm  [stored 1.15486 ft] | 688 mm  [stored 2.25722 ft] | 4 | 652 mm  [stored 2.13911 ft] | 318 mm  [stored 1.04331 ft] | 12 | No | Yes | Yes | VF412PD | 4 | 12 |
| GOLF-Flush_mounted_W352_H688_D97_12_Modular_Spacing-VF412PJ | {"ObjectGuid":"2e7d348a-37d7-415c-a700-8c675d7a2511","ModelGuid":"d92884ee-31d5-45f1-a563-37bca790122f","VariantGuid":"23207760-10b2-4df7-90f7-609229f90366","Revision":"#5","VariantName":"GOLF-Flush_mounted_W352_H688_D97_12_Modular_Spacing-VF412PJ"} | 352 mm  [stored 1.15486 ft] | 688 mm  [stored 2.25722 ft] | 4 | 652 mm  [stored 2.13911 ft] | 318 mm  [stored 1.04331 ft] | 12 | No | Yes | Yes | VF412PJ | 4 | 12 |
| GOLF-Flush_mounted_W352_H688_D97_12_Modular_Spacing-VF412PS | {"ObjectGuid":"2e7d348a-37d7-415c-a700-8c675d7a2511","ModelGuid":"d92884ee-31d5-45f1-a563-37bca790122f","VariantGuid":"2fe7caaf-29e4-46e8-bbdc-5e274c7c35a9","Revision":"#5","VariantName":"GOLF-Flush_mounted_W352_H688_D97_12_Modular_Spacing-VF412PS"} | 352 mm  [stored 1.15486 ft] | 688 mm  [stored 2.25722 ft] | 4 | 652 mm  [stored 2.13911 ft] | 318 mm  [stored 1.04331 ft] | 12 | No | Yes | Yes | VF412PS | 4 | 12 |
| GOLF-Flush_mounted_W352_H688_D97_12_Modular_Spacing-VF412TD | {"ObjectGuid":"2e7d348a-37d7-415c-a700-8c675d7a2511","ModelGuid":"d92884ee-31d5-45f1-a563-37bca790122f","VariantGuid":"5203e280-b7b0-4cc0-a619-52bf8acbade6","Revision":"#5","VariantName":"GOLF-Flush_mounted_W352_H688_D97_12_Modular_Spacing-VF412TD"} | 352 mm  [stored 1.15486 ft] | 688 mm  [stored 2.25722 ft] | 4 | 652 mm  [stored 2.13911 ft] | 318 mm  [stored 1.04331 ft] | 12 | Yes | Yes | Yes | VF412TD | 4 | 12 |
| GOLF-Flush_mounted_W352_H688_D97_12_Modular_Spacing-VF412TJ | {"ObjectGuid":"2e7d348a-37d7-415c-a700-8c675d7a2511","ModelGuid":"d92884ee-31d5-45f1-a563-37bca790122f","VariantGuid":"398e9fe3-fbfb-4845-8cde-18893fabaa41","Revision":"#5","VariantName":"GOLF-Flush_mounted_W352_H688_D97_12_Modular_Spacing-VF412TJ"} | 352 mm  [stored 1.15486 ft] | 688 mm  [stored 2.25722 ft] | 4 | 652 mm  [stored 2.13911 ft] | 318 mm  [stored 1.04331 ft] | 12 | Yes | Yes | Yes | VF412TJ | 4 | 12 |
| GOLF-Flush_mounted_W352_H688_D97_12_Modular_Spacing-VF412TS | {"ObjectGuid":"2e7d348a-37d7-415c-a700-8c675d7a2511","ModelGuid":"d92884ee-31d5-45f1-a563-37bca790122f","VariantGuid":"e540b39a-cbf7-45bd-a877-693dadfeae98","Revision":"#5","VariantName":"GOLF-Flush_mounted_W352_H688_D97_12_Modular_Spacing-VF412TS"} | 352 mm  [stored 1.15486 ft] | 688 mm  [stored 2.25722 ft] | 4 | 652 mm  [stored 2.13911 ft] | 318 mm  [stored 1.04331 ft] | 12 | Yes | Yes | Yes | VF412TS | 4 | 12 |
| GOLF-Flush_mounted_W460_H688_D97_18_Modular_Spacing-VF418PD | {"ObjectGuid":"2e7d348a-37d7-415c-a700-8c675d7a2511","ModelGuid":"d92884ee-31d5-45f1-a563-37bca790122f","VariantGuid":"0f819dfe-817d-4e2a-8253-5f57dc6628f3","Revision":"#5","VariantName":"GOLF-Flush_mounted_W460_H688_D97_18_Modular_Spacing-VF418PD"} | 460 mm  [stored 1.50919 ft] | 688 mm  [stored 2.25722 ft] | 4 | 652 mm  [stored 2.13911 ft] | 426 mm  [stored 1.39764 ft] | 18 | No | Yes | Yes | VF418PD | 4 | 18 |
| GOLF-Flush_mounted_W460_H688_D97_18_Modular_Spacing-VF418PJ | {"ObjectGuid":"2e7d348a-37d7-415c-a700-8c675d7a2511","ModelGuid":"d92884ee-31d5-45f1-a563-37bca790122f","VariantGuid":"857a56e2-ad4f-45ed-8842-008f0a8a2a7a","Revision":"#5","VariantName":"GOLF-Flush_mounted_W460_H688_D97_18_Modular_Spacing-VF418PJ"} | 460 mm  [stored 1.50919 ft] | 688 mm  [stored 2.25722 ft] | 4 | 652 mm  [stored 2.13911 ft] | 426 mm  [stored 1.39764 ft] | 18 | No | Yes | Yes | VF418PJ | 4 | 18 |
| GOLF-Flush_mounted_W460_H688_D97_18_Modular_Spacing-VF418PS | {"ObjectGuid":"2e7d348a-37d7-415c-a700-8c675d7a2511","ModelGuid":"d92884ee-31d5-45f1-a563-37bca790122f","VariantGuid":"27995be1-88a8-4d9a-88e0-36cd34742173","Revision":"#5","VariantName":"GOLF-Flush_mounted_W460_H688_D97_18_Modular_Spacing-VF418PS"} | 460 mm  [stored 1.50919 ft] | 688 mm  [stored 2.25722 ft] | 4 | 652 mm  [stored 2.13911 ft] | 426 mm  [stored 1.39764 ft] | 18 | No | Yes | Yes | VF418PS | 4 | 18 |
| GOLF-Flush_mounted_W460_H688_D97_18_Modular_Spacing-VF418TD | {"ObjectGuid":"2e7d348a-37d7-415c-a700-8c675d7a2511","ModelGuid":"d92884ee-31d5-45f1-a563-37bca790122f","VariantGuid":"4e823974-3b67-4a63-8b77-92549911597c","Revision":"#5","VariantName":"GOLF-Flush_mounted_W460_H688_D97_18_Modular_Spacing-VF418TD"} | 460 mm  [stored 1.50919 ft] | 688 mm  [stored 2.25722 ft] | 4 | 652 mm  [stored 2.13911 ft] | 426 mm  [stored 1.39764 ft] | 18 | Yes | Yes | Yes | VF418TD | 4 | 18 |
| GOLF-Flush_mounted_W460_H688_D97_18_Modular_Spacing-VF418TJ | {"ObjectGuid":"2e7d348a-37d7-415c-a700-8c675d7a2511","ModelGuid":"d92884ee-31d5-45f1-a563-37bca790122f","VariantGuid":"358fd311-be00-4c3c-8eda-2190eeab5305","Revision":"#5","VariantName":"GOLF-Flush_mounted_W460_H688_D97_18_Modular_Spacing-VF418TJ"} | 460 mm  [stored 1.50919 ft] | 688 mm  [stored 2.25722 ft] | 4 | 652 mm  [stored 2.13911 ft] | 426 mm  [stored 1.39764 ft] | 18 | Yes | Yes | Yes | VF418TJ | 4 | 18 |
| GOLF-Flush_mounted_W460_H688_D97_18_Modular_Spacing-VF418TS | {"ObjectGuid":"2e7d348a-37d7-415c-a700-8c675d7a2511","ModelGuid":"d92884ee-31d5-45f1-a563-37bca790122f","VariantGuid":"0a333e97-2d78-4972-93eb-309a8a41e19d","Revision":"#5","VariantName":"GOLF-Flush_mounted_W460_H688_D97_18_Modular_Spacing-VF418TS"} | 460 mm  [stored 1.50919 ft] | 688 mm  [stored 2.25722 ft] | 4 | 652 mm  [stored 2.13911 ft] | 426 mm  [stored 1.39764 ft] | 18 | Yes | Yes | Yes | VF418TS | 4 | 18 |

note: [stored X ft] marks values corroborated as IEEE doubles in the binary element streams (Revit-internal decimal feet)

## geometry (parser evidence)
native form markers: Sweep x14
no freeform markers — native parametric forms only
